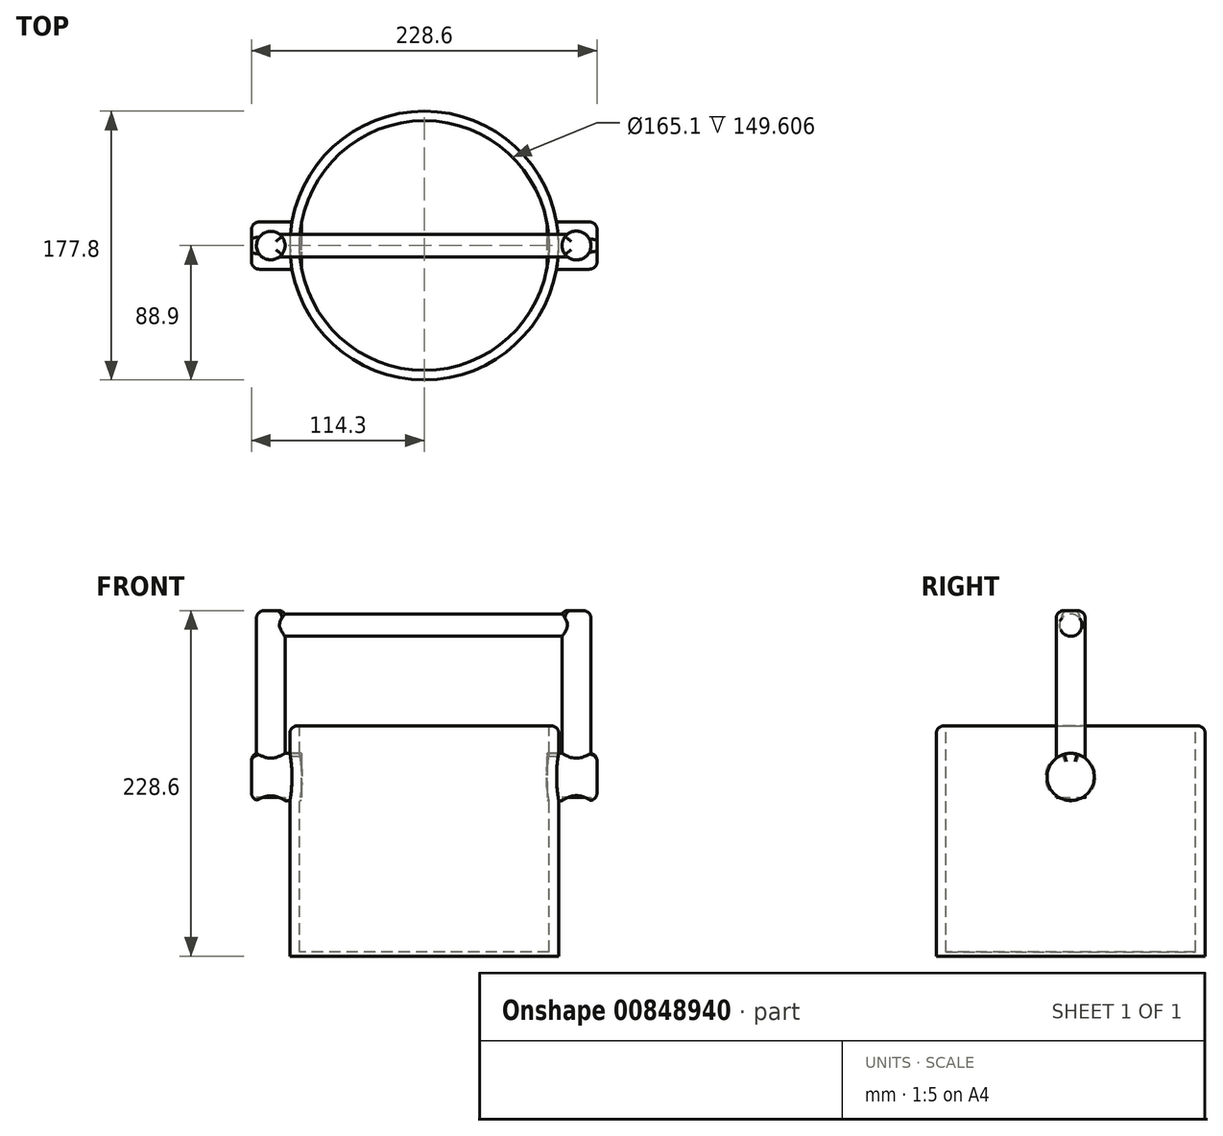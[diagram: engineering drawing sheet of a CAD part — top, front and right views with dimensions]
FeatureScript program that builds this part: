
annotation { "Feature Type Name" : "Feature", "Feature Type Description" : "" }
export const myFeature = defineFeature(function(context is Context, id is Id, definition is map)
    precondition{}
    {
        {
            var Q0;
            Q0=qCreatedBy(makeId("Top.planeOp"),FACE);
            var sketch = newSketch(context, id + "F0", { "sketchPlane" : qUnion([Q0])});
            skCircle(sketch, "E0", {"center": v(0, 0) * mm, "radius": 88.9 * mm});
            skSolve(sketch);
        }
        {
            var Q0;
            Q0=makeQuery(id+"F0.imprint","IMPRINT",FACE,{"disambiguationData":[TD([[makeQuery(id+"F0.imprint","IMPRINT",EDGE,{"derivedFrom":sQuery(id+"F0.wireOp",EDGE,"E0")}),1.0]])]});
            extrude(context, id + "F1", {"entities" : qUnion([Q0]), "depth" : 76.2 * mm, "offsetDistance" : 25.4 * mm, "hasSecondDirection" : true, "secondDirectionOppositeDirection" : true, "secondDirectionDepth" : 76.2 * mm});
        }
        {
            var Q0;
            Q0=makeQuery(id+"F1.opExtrude","CAP_FACE",FACE,{"disambiguationData":[OSD([sQuery(id+"F0.wireOp",EDGE,"E0")])],"isStart":false});
            var sketch = newSketch(context, id + "F2", { "sketchPlane" : qUnion([Q0])});
            skCircle(sketch, "E1", {"center": v(0, 0) * mm, "radius": 82.55 * mm});
            skSolve(sketch);
        }
        {
            var Q0;
            Q0=makeQuery(id+"F2.imprint","IMPRINT",FACE,{"disambiguationData":[TD([[makeQuery(id+"F2.imprint","IMPRINT",EDGE,{"derivedFrom":sQuery(id+"F2.wireOp",EDGE,"E1")}),1.0]])]});
            extrude(context, id + "F3", {"entities" : qUnion([Q0]), "operationType" : NewBodyOperationType.REMOVE, "oppositeDirection" : true, "depth" : 149.6 * mm, "offsetDistance" : 25.4 * mm});
        }
        {
            var Q0;
            Q0=qCreatedBy(makeId("Right.planeOp"),FACE);
            var sketch = newSketch(context, id + "F4", { "sketchPlane" : qUnion([Q0])});
            skCircle(sketch, "E2", {"center": v(0, 43.02) * mm, "radius": 15.02 * mm});
            skSolve(sketch);
        }
        {
            var Q0;
            Q0=qSketchRegion(id+"F4",true);
            extrude(context, id + "F5", {"entities" : qUnion([Q0]), "operationType" : NewBodyOperationType.REMOVE, "surfaceOperationType" : NewSurfaceOperationType.ADD, "endBound" : BoundingType.THROUGH_ALL, "oppositeDirection" : true, "depth" : 25.4 * mm, "offsetDistance" : 25.4 * mm, "hasSecondDirection" : true, "secondDirectionOppositeDirection" : false, "secondDirectionDepth" : 95 * mm});
        }
        {
            var Q0;
            Q0=qCreatedBy(makeId("Right.planeOp"),FACE);
            var sketch = newSketch(context, id + "F6", { "sketchPlane" : qUnion([Q0])});
            skCircle(sketch, "E3", {"center": v(0, 42.31) * mm, "radius": 15.63 * mm});
            skSolve(sketch);
        }
        {
            var Q0;
            Q0=qSketchRegion(id+"F6",true);
            extrude(context, id + "F7", {"entities" : qUnion([Q0]), "operationType" : NewBodyOperationType.ADD, "surfaceOperationType" : NewSurfaceOperationType.ADD, "depth" : 114.3 * mm, "offsetDistance" : 25.4 * mm, "hasSecondDirection" : true, "secondDirectionOppositeDirection" : true, "secondDirectionDepth" : 114.3 * mm});
        }
        {
            var Q0;
            Q0=qCreatedBy(makeId("Right.planeOp"),FACE);
            var sketch = newSketch(context, id + "F8", { "sketchPlane" : qUnion([Q0])});
            skCircle(sketch, "E4", {"center": v(-0.17, 42.23) * mm, "radius": 16.62 * mm});
            skPoint(sketch, "E4.first.point", {"position": v(8.02, 56.69) * mm});
            skPoint(sketch, "E4.second.point", {"position": v(6.91, 27.2) * mm});
            skPoint(sketch, "E4.third.point", {"position": v(-14.29, 33.46) * mm});
            skSolve(sketch);
        }
        {
            var Q0;
            Q0=qSketchRegion(id+"F8",true);
            extrude(context, id + "F9", {"entities" : qUnion([Q0]), "operationType" : NewBodyOperationType.REMOVE, "oppositeDirection" : true, "depth" : 81.28 * mm, "offsetDistance" : 25.4 * mm, "hasSecondDirection" : true, "secondDirectionOppositeDirection" : false, "secondDirectionDepth" : 81.28 * mm});
        }
        {
            var Q0;
            Q0=qCreatedBy(makeId("Top.planeOp"),FACE);
            var sketch = newSketch(context, id + "F10", { "sketchPlane" : qUnion([Q0])});
            skCircle(sketch, "E5", {"center": v(-101.57, 0) * mm, "radius": 9.43 * mm});
            skSolve(sketch);
        }
        {
            var Q0;
            Q0=qSketchRegion(id+"F10",true);
            extrude(context, id + "F11", {"entities" : qUnion([Q0]), "operationType" : NewBodyOperationType.ADD, "surfaceOperationType" : NewSurfaceOperationType.ADD, "depth" : 152.4 * mm, "offsetDistance" : 25.4 * mm});
        }
        {
            var Q0;
            Q0=makeQuery(id+"F11.opExtrude","CAP_FACE",FACE,{"disambiguationData":[OSD([sQuery(id+"F10.wireOp",EDGE,"E5")])],"isStart":true});
            extrude(context, id + "F12", {"entities" : qUnion([Q0]), "operationType" : NewBodyOperationType.REMOVE, "oppositeDirection" : true, "depth" : 28.7 * mm, "offsetDistance" : 25.4 * mm});
        }
        {
            var Q0;
            Q0=qCreatedBy(makeId("Top.planeOp"),FACE);
            var sketch = newSketch(context, id + "F13", { "sketchPlane" : qUnion([Q0])});
            skCircle(sketch, "E6", {"center": v(100.69, 0) * mm, "radius": 9.55 * mm});
            skSolve(sketch);
        }
        {
            var Q0;
            Q0=qSketchRegion(id+"F13",true);
            extrude(context, id + "F14", {"entities" : qUnion([Q0]), "operationType" : NewBodyOperationType.ADD, "depth" : 152.4 * mm, "offsetDistance" : 25.4 * mm});
        }
        {
            var Q0;
            Q0=makeQuery(id+"F14.opExtrude","CAP_FACE",FACE,{"disambiguationData":[OSD([sQuery(id+"F13.wireOp",EDGE,"E6")])],"isStart":true});
            extrude(context, id + "F15", {"entities" : qUnion([Q0]), "operationType" : NewBodyOperationType.REMOVE, "oppositeDirection" : true, "depth" : 28.7 * mm, "offsetDistance" : 25.4 * mm});
        }
        {
            var Q0;
            Q0=qCreatedBy(makeId("Right.planeOp"),FACE);
            var sketch = newSketch(context, id + "F16", { "sketchPlane" : qUnion([Q0])});
            skCircle(sketch, "E7", {"center": v(0, 142.77) * mm, "radius": 7.44 * mm});
            skSolve(sketch);
        }
        {
            var Q0;
            Q0=qSketchRegion(id+"F16",true);
            extrude(context, id + "F17", {"entities" : qUnion([Q0]), "operationType" : NewBodyOperationType.ADD, "depth" : 101.6 * mm, "offsetDistance" : 25.4 * mm, "hasSecondDirection" : true, "secondDirectionOppositeDirection" : true, "secondDirectionDepth" : 101.6 * mm});
        }
        {
            var Q0;
            Q0=makeQuery(id+"F11.opExtrude","CAP_EDGE",EDGE,{"disambiguationData":[OSD([sQuery(id+"F10.wireOp",EDGE,"E5")])],"isStart":false});
            var Q1;
            Q1=makeQuery(id+"F14.opExtrude","CAP_EDGE",EDGE,{"disambiguationData":[OSD([sQuery(id+"F13.wireOp",EDGE,"E6")])],"isStart":false});
            var Q2;
            Q2=makeQuery(id+"F7.opExtrude","CAP_EDGE",EDGE,{"disambiguationData":[OSD([sQuery(id+"F6.wireOp",EDGE,"E3")])],"isStart":false});
            var Q3;
            Q3=makeQuery(id+"F7.opExtrude","CAP_EDGE",EDGE,{"disambiguationData":[OSD([sQuery(id+"F6.wireOp",EDGE,"E3")])],"isStart":true});
            var Q4;
            Q4=makeQuery(id+"F1.opExtrude","CAP_EDGE",EDGE,{"disambiguationData":[OSD([sQuery(id+"F0.wireOp",EDGE,"E0")])],"isStart":false});
            fillet(context, id + "F18", {"entities" : qUnion([Q0, Q1, Q2, Q3, Q4]), "radius" : 5.08 * mm, "tangentPropagation" : true, "allowEdgeOverflow" : false});
        }
    });
